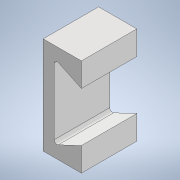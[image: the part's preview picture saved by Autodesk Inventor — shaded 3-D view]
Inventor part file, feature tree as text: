
AUTODESK INVENTOR PART (.ipt)
format: ipt  version: 2022 (Build 260153000, 153)  size: 116,224 bytes
history: native  units: mm
features: other x3, extrude x1, fillet x1, sketch x1, reference x1
ambient origin geometry x8: Origin, YZ Plane, XZ Plane, XY Plane, X Axis, Y Axis, Z Axis, Center Point
bodies: Solid1 (feature_tree)
feature tree (7):
  extrude  "Extrusion1"  Depth=1.0mm
  fillet  "Fillet1"  Radius=0.2mm
  sketch  "Sketch1"  dims[d0=0.2mm d1=0.2mm d2=0.2mm d3=2.0mm d4=2.0mm d5=10.0mm d6=0.0mm d7=1.0mm]
  reference  "Reference1"
  other  "<userpath>\OneDrive - Imperial College London\ROBOICP MK2\solids feeder assembly.iam"
  other  "solids feeder assembly.iam"
  other  "screw_casing:1"
